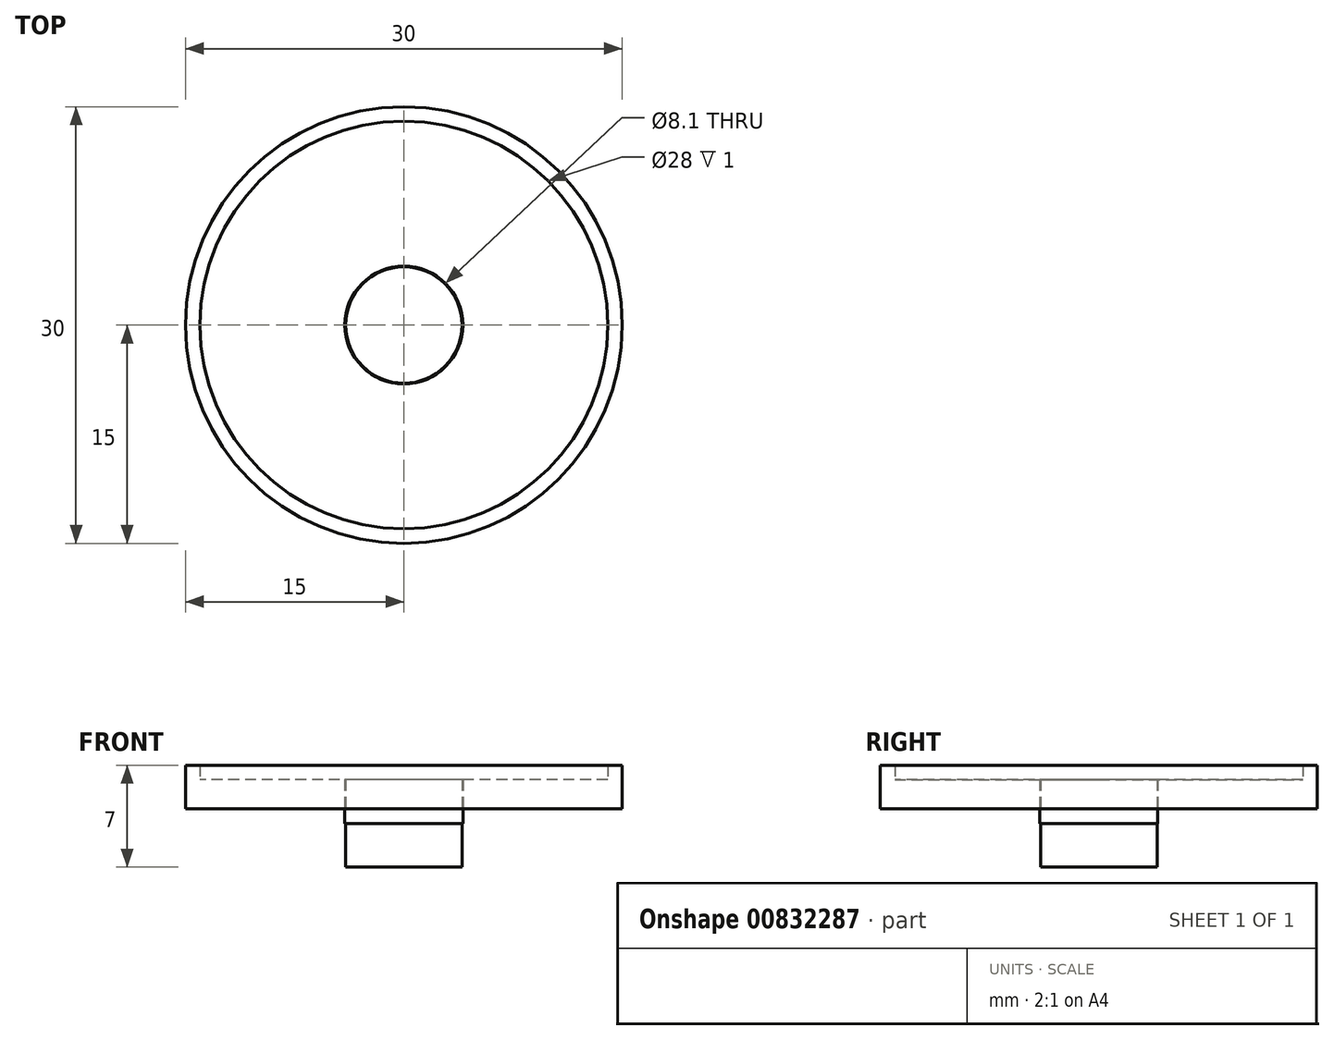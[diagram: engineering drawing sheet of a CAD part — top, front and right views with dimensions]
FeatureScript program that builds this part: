
annotation { "Feature Type Name" : "Feature", "Feature Type Description" : "" }
export const myFeature = defineFeature(function(context is Context, id is Id, definition is map)
    precondition{}
    {
        {
            var Q0;
            Q0=qCreatedBy(makeId("Top.planeOp"),FACE);
            var sketch = newSketch(context, id + "F0", { "sketchPlane" : qUnion([Q0])});
            skCircle(sketch, "E0", {"center": v(0, 0) * mm, "radius": 4 * mm});
            skCircle(sketch, "E1", {"center": v(0, 0) * mm, "radius": 4.05 * mm});
            skCircle(sketch, "E2", {"center": v(0, 0) * mm, "radius": 11 * mm});
            skCircle(sketch, "E3", {"center": v(0, 0) * mm, "radius": 15 * mm});
            skCircle(sketch, "E4", {"center": v(0, 0) * mm, "radius": 14 * mm});
            skSolve(sketch);
        }
        {
            var Q0;
            Q0=makeQuery(id+"F0.imprint","IMPRINT",FACE,{"disambiguationData":[TD([[makeQuery(id+"F0.imprint","IMPRINT",EDGE,{"derivedFrom":sQuery(id+"F0.wireOp",EDGE,"E0")}),1.0]])]});
            extrude(context, id + "F1", {"entities" : qUnion([Q0]), "oppositeDirection" : true, "depth" : 4 * mm, "offsetDistance" : 25 * mm});
        }
        {
            var Q0;
            Q0=makeQuery(id+"F0.imprint","IMPRINT",FACE,{"disambiguationData":[TD([[makeQuery(id+"F0.imprint","IMPRINT",EDGE,{"derivedFrom":sQuery(id+"F0.wireOp",EDGE,"E0")}),-1.0]])]});
            extrude(context, id + "F2", {"entities" : qUnion([Q0]), "oppositeDirection" : true, "depth" : 1 * mm, "offsetDistance" : 25 * mm});
        }
        {
            var Q0;
            Q0=makeQuery(id+"F0.imprint","IMPRINT",FACE,{"disambiguationData":[TD([[makeQuery(id+"F0.imprint","IMPRINT",EDGE,{"derivedFrom":sQuery(id+"F0.wireOp",EDGE,"E0")}),1.0]])]});
            var Q1;
            Q1=makeQuery(id+"F0.imprint","IMPRINT",FACE,{"disambiguationData":[TD([[makeQuery(id+"F0.imprint","IMPRINT",EDGE,{"derivedFrom":sQuery(id+"F0.wireOp",EDGE,"E1")}),-1.0]])]});
            var Q2;
            Q2=makeQuery(id+"F0.imprint","IMPRINT",FACE,{"disambiguationData":[TD([[makeQuery(id+"F0.imprint","IMPRINT",EDGE,{"derivedFrom":sQuery(id+"F0.wireOp",EDGE,"E2")}),-1.0]])]});
            var Q3;
            Q3=makeQuery(id+"F0.imprint","IMPRINT",FACE,{"disambiguationData":[TD([[makeQuery(id+"F0.imprint","IMPRINT",EDGE,{"derivedFrom":sQuery(id+"F0.wireOp",EDGE,"E3")}),1.0]])]});
            extrude(context, id + "F3", {"entities" : qUnion([Q0, Q1, Q2, Q3]), "operationType" : NewBodyOperationType.ADD, "depth" : 2 * mm, "offsetDistance" : 25 * mm});
        }
        {
            var Q0;
            Q0=makeQuery(id+"F0.imprint","IMPRINT",FACE,{"disambiguationData":[TD([[makeQuery(id+"F0.imprint","IMPRINT",EDGE,{"derivedFrom":sQuery(id+"F0.wireOp",EDGE,"E3")}),1.0]])]});
            extrude(context, id + "F4", {"entities" : qUnion([Q0]), "operationType" : NewBodyOperationType.ADD, "depth" : 3 * mm, "offsetDistance" : 25 * mm});
        }
    });
